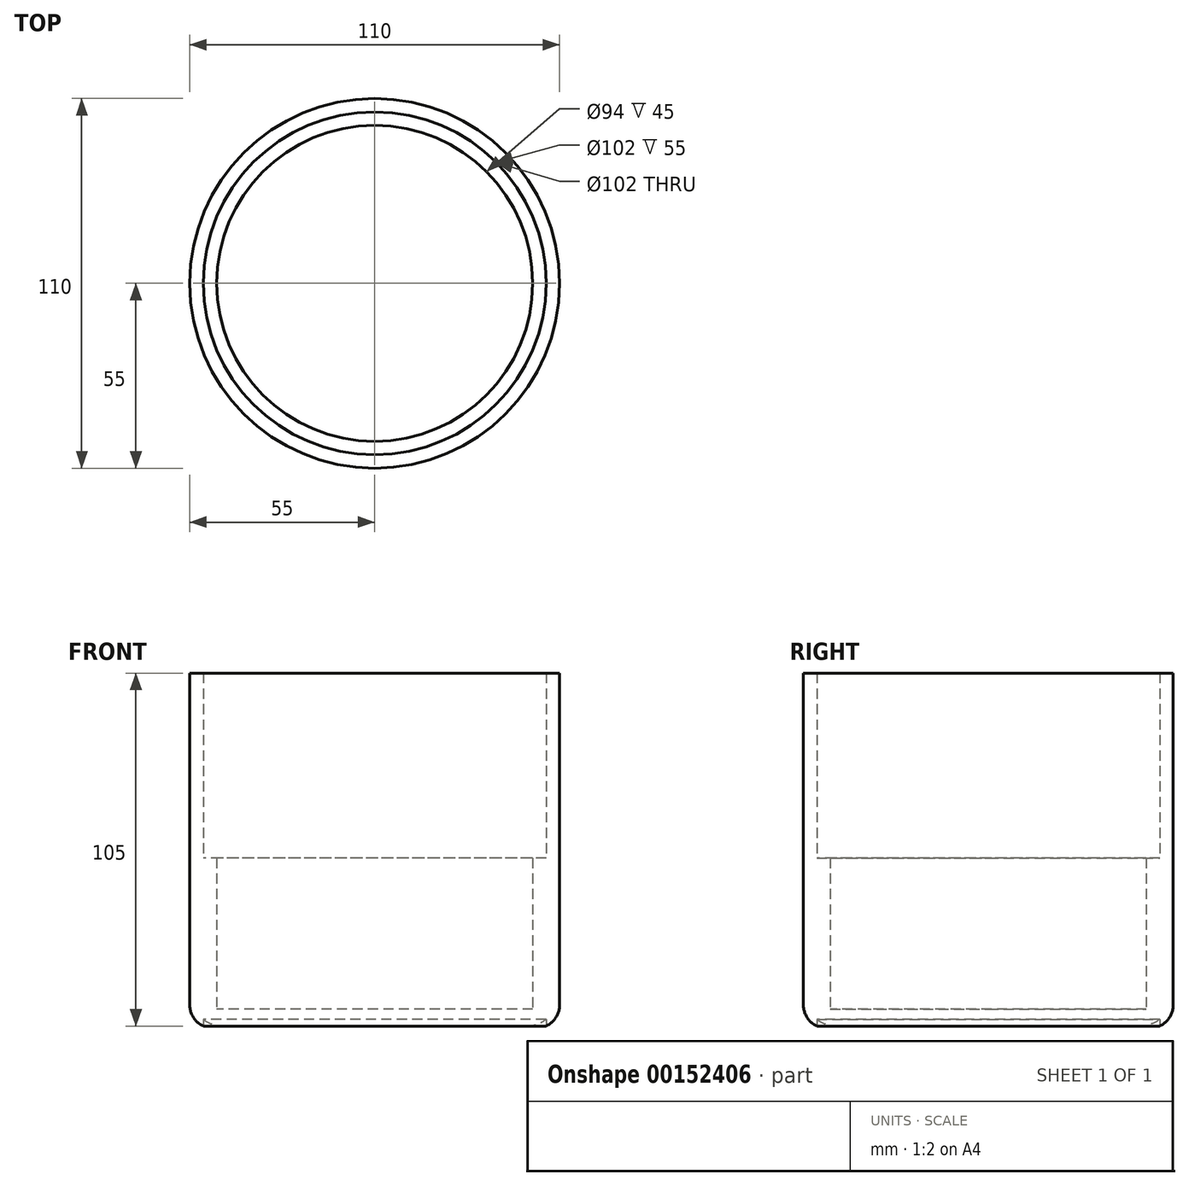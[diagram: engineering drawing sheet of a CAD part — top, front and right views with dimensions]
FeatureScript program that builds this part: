
annotation { "Feature Type Name" : "Feature", "Feature Type Description" : "" }
export const myFeature = defineFeature(function(context is Context, id is Id, definition is map)
    precondition{}
    {
        {
            var Q0;
            Q0=qCreatedBy(makeId("Top.planeOp"),FACE);
            var sketch = newSketch(context, id + "F0", { "sketchPlane" : qUnion([Q0])});
            skCircle(sketch, "E0", {"center": v(0, 0) * mm, "radius": 51 * mm});
            skCircle(sketch, "E1", {"center": v(0, 0) * mm, "radius": 47 * mm});
            skCircle(sketch, "E2", {"center": v(0, 0) * mm, "radius": 55 * mm});
            skSolve(sketch);
        }
        {
            var Q0;
            Q0=makeQuery(id+"F0.imprint","IMPRINT",FACE,{"disambiguationData":[TD([[makeQuery(id+"F0.imprint","IMPRINT",EDGE,{"derivedFrom":sQuery(id+"F0.wireOp",EDGE,"E0")}),-1.0]])]});
            var Q1;
            Q1=makeQuery(id+"F0.imprint","IMPRINT",FACE,{"disambiguationData":[TD([[makeQuery(id+"F0.imprint","IMPRINT",EDGE,{"derivedFrom":sQuery(id+"F0.wireOp",EDGE,"E0")}),1.0]])]});
            var Q2;
            Q2=makeQuery(id+"F0.imprint","IMPRINT",FACE,{"disambiguationData":[TD([[makeQuery(id+"F0.imprint","IMPRINT",EDGE,{"derivedFrom":sQuery(id+"F0.wireOp",EDGE,"E1")}),1.0]])]});
            extrude(context, id + "F1", {"entities" : qUnion([Q0, Q1, Q2]), "depth" : 5 * mm});
        }
        {
            var Q0;
            Q0=makeQuery(id+"F0.imprint","IMPRINT",FACE,{"disambiguationData":[TD([[makeQuery(id+"F0.imprint","IMPRINT",EDGE,{"derivedFrom":sQuery(id+"F0.wireOp",EDGE,"E0")}),1.0]])]});
            extrude(context, id + "F2", {"entities" : qUnion([Q0]), "operationType" : NewBodyOperationType.ADD, "depth" : 50 * mm});
        }
        {
            var Q0;
            {var subQ0=sQuery(id+"F0.wireOp",EDGE,"E2");Q0=makeQuery(id+"F2.boolean.opBoolean","SPLIT",FACE,{"disambiguationData":[TD([makeQuery(id+"F1.opExtrude","SWEPT_FACE",FACE,{"disambiguationData":[OSD([subQ0])]})])],"derivedFrom":makeQuery(id+"F1.opExtrude","CAP_FACE",FACE,{"disambiguationData":[OSD([subQ0])],"isStart":false})});}
            extrude(context, id + "F3", {"entities" : qUnion([Q0]), "operationType" : NewBodyOperationType.ADD, "depth" : 100 * mm});
        }
        {
            var Q0;
            Q0=makeQuery(id+"F1.opExtrude","CAP_EDGE",EDGE,{"disambiguationData":[OSD([sQuery(id+"F0.wireOp",EDGE,"E2")])],"isStart":true});
            fillet(context, id + "F4", {"entities" : qUnion([Q0]), "radius" : 10 * mm, "tangentPropagation" : true, "allowEdgeOverflow" : false});
        }
        {
            var Q0;
            Q0 = qSketchRegion(id + "F0", true);
            extrude(context, id + "F5", {"entities" : qUnion([Q0]), "operationType" : NewBodyOperationType.ADD, "depth" : 25 * mm});
        }
        {
            var Q0;
            Q0 = qSketchRegion(id + "F0", true);
            extrude(context, id + "F6", {"entities" : qUnion([Q0]), "operationType" : NewBodyOperationType.ADD, "depth" : 25 * mm});
        }
        {
            var Q0;
            Q0 = qSketchRegion(id + "F0", true);
            extrude(context, id + "F7", {"entities" : qUnion([Q0]), "operationType" : NewBodyOperationType.ADD, "depth" : 25 * mm});
        }
        {
            var Q0;
            Q0=makeQuery(id+"F5.opExtrude","CAP_EDGE",EDGE,{"disambiguationData":[OSD([sQuery(id+"F0.wireOp",EDGE,"E2")])],"isStart":true});
            fillet(context, id + "F8", {"entities" : qUnion([Q0]), "radius" : 7 * mm, "tangentPropagation" : true, "allowEdgeOverflow" : false});
        }
    });
